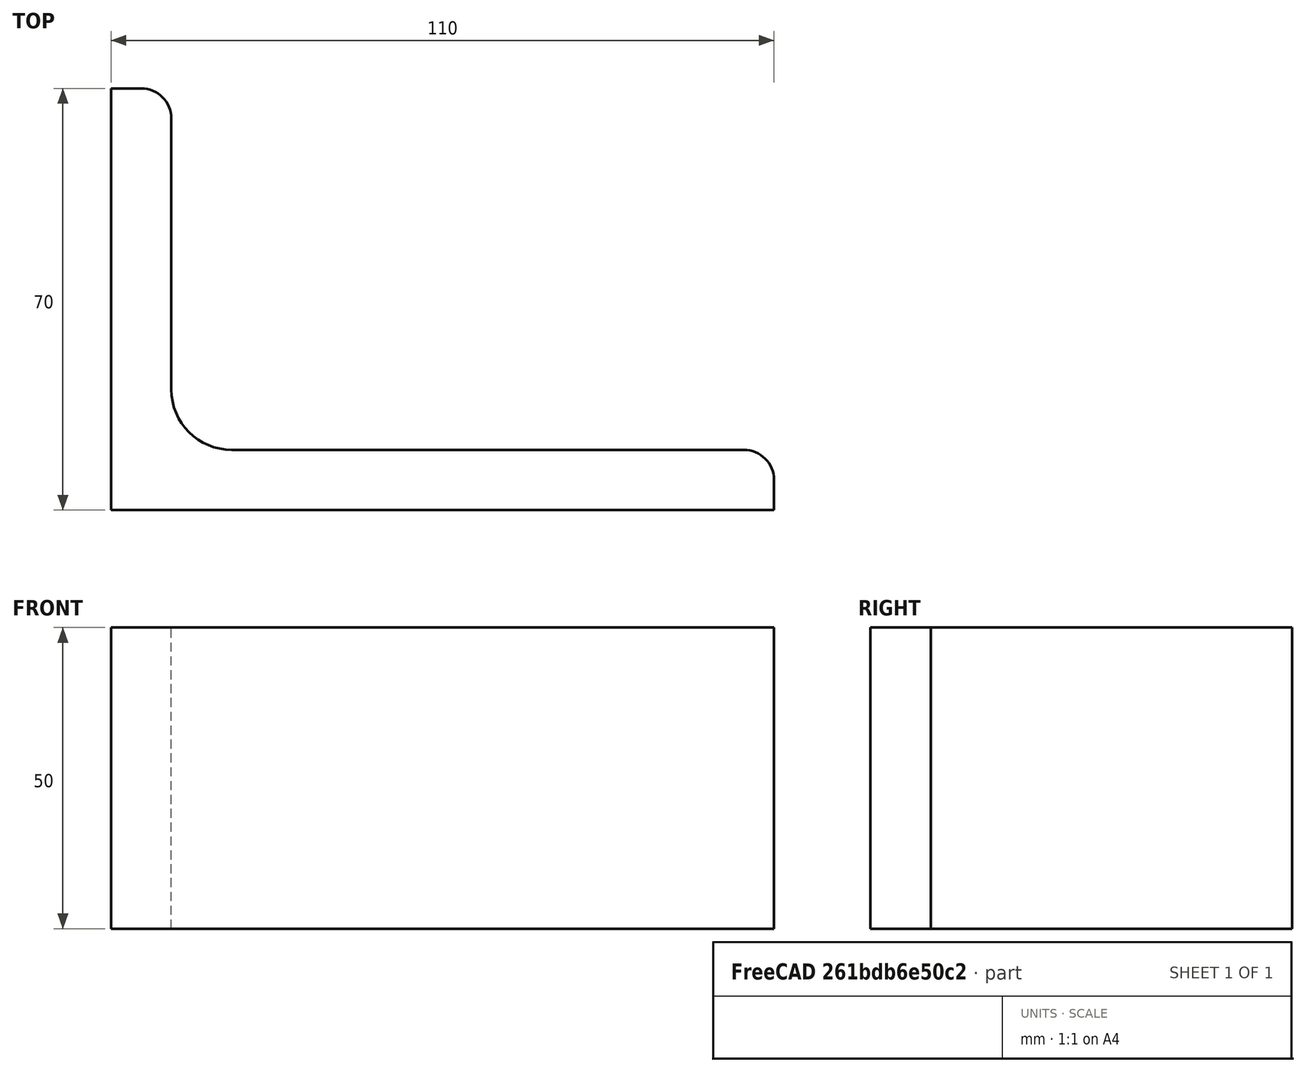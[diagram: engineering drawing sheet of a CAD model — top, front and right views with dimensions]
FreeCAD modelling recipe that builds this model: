
FCSTD DOCUMENT  (FreeCAD 0.15R4671 (Git))
Label: Angle Bar 110x70x10 EN10056 S235JR
License: All rights reserved
LicenseURL: http://en.wikipedia.org/wiki/All_rights_reserved
objects: Sketcher::SketchObject×1, Part::Extrusion×1
note: 2 computed .brp shape members not serialized (recipe doc carries the construction recipe); baked Part::Feature solids carry a one-line shape summary decoded from their .brp

FEATURE [Sketcher::SketchObject] Sketch
  sketch-geometry (9):
    g0: LineSegment StartX=0 StartY=0 StartZ=0 EndX=110 EndY=0 EndZ=0
    g1: LineSegment StartX=110 StartY=0 StartZ=0 EndX=110 EndY=5 EndZ=0
    g2: LineSegment StartX=105 StartY=10 StartZ=0 EndX=20 EndY=10 EndZ=0
    g3: LineSegment StartX=0 StartY=0 StartZ=0 EndX=0 EndY=70 EndZ=0
    g4: LineSegment StartX=0 StartY=70 StartZ=0 EndX=5 EndY=70 EndZ=0
    g5: LineSegment StartX=10 StartY=65 StartZ=0 EndX=10 EndY=20 EndZ=0
    g6: ArcOfCircle CenterX=20 CenterY=20 CenterZ=0 NormalX=0 NormalY=0 NormalZ=1 Radius=10 StartAngle=3.14159 EndAngle=4.71239
    g7: ArcOfCircle CenterX=5 CenterY=65 CenterZ=0 NormalX=0 NormalY=0 NormalZ=1 Radius=5 StartAngle=0 EndAngle=1.5708
    g8: ArcOfCircle CenterX=105 CenterY=5 CenterZ=0 NormalX=0 NormalY=0 NormalZ=1 Radius=5 StartAngle=0 EndAngle=1.5708
  constraints (23):
    c: Coincident(g0,g-1)
    c: Horizontal(g0)
    c: Coincident(g1,g0)
    c: Vertical(g1)
    c: Horizontal(g2)
    c: Coincident(g3,g-1)
    c: Vertical(g3)
    c: Coincident(g4,g3)
    c: Horizontal(g4)
    c: Vertical(g5)
    c: Tangent(g5,g6) = -1.5708
    c: Tangent(g2,g6) = 1.5708
    c: Tangent(g4,g7) = 1.5708
    c: Tangent(g5,g7) = 1.5708
    c: Tangent(g2,g8) = -1.5708
    c: Tangent(g1,g8) = -1.5708
    c: DistanceX(g0) = 110
    c: DistanceY(g3) = 70
    c: DistanceY(g0,g2) = 10
    c: DistanceX(g3,g5) = 10
    c: Radius(g6) = 10
    c: Radius(g8) = 5
    c: Radius(g7) = 5
FEATURE [Part::Extrusion] Extrude  label="Angle Bar 110x70x10 EN10056 S235JR"
  Base = -> Sketch
  Dir = (0,0,50)
  Solid = true
